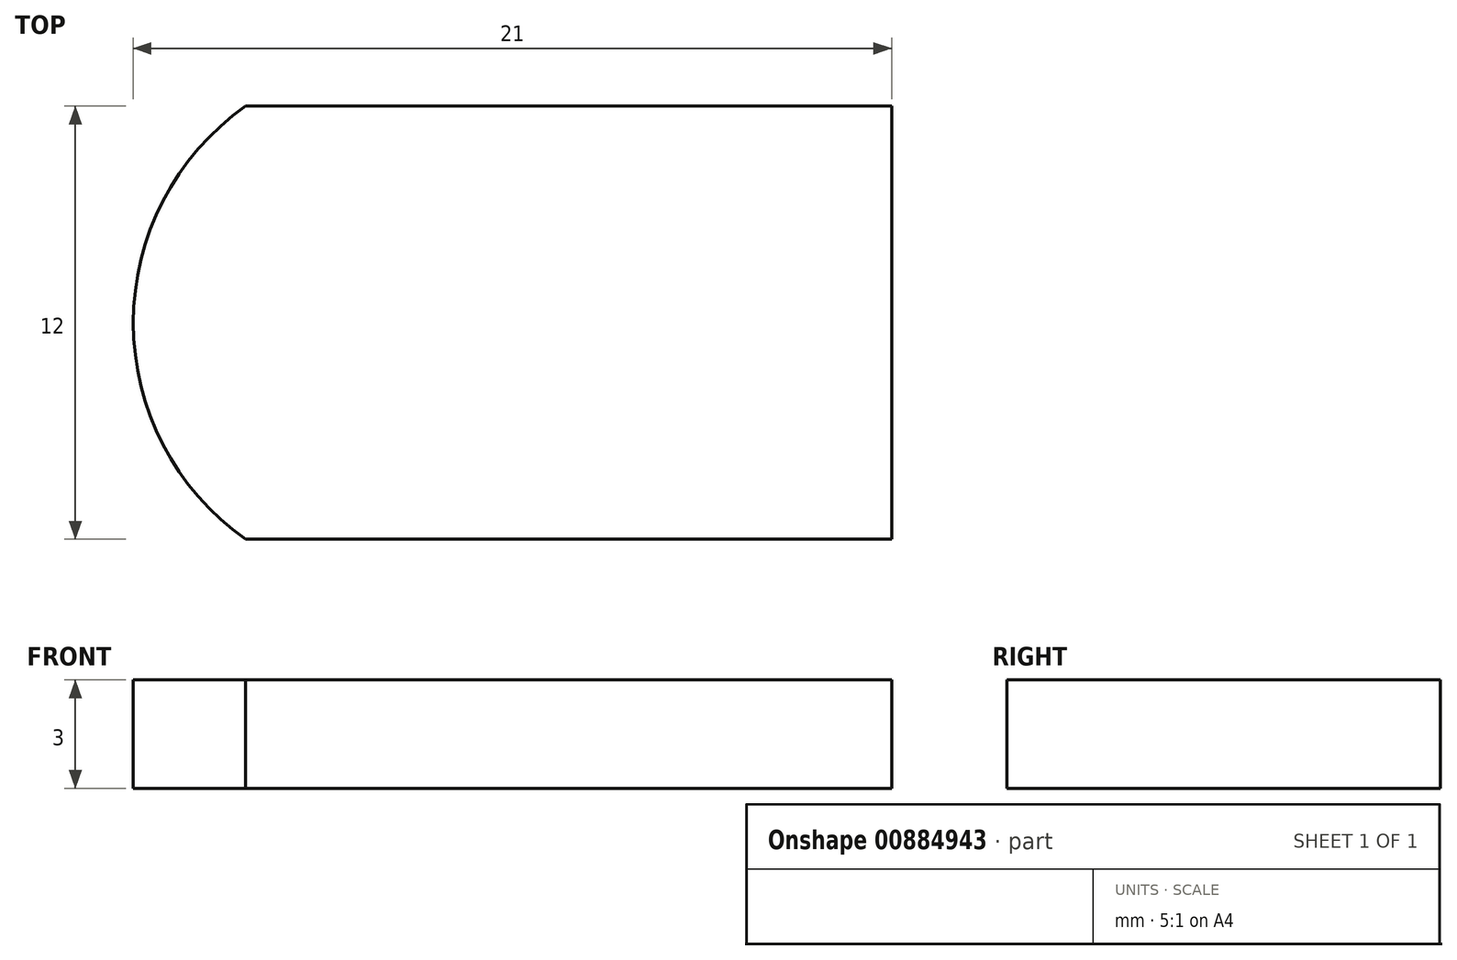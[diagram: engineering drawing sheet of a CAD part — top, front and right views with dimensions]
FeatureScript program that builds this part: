
annotation { "Feature Type Name" : "Feature", "Feature Type Description" : "" }
export const myFeature = defineFeature(function(context is Context, id is Id, definition is map)
    precondition{}
    {
        {
            var Q0;
            Q0=qCreatedBy(makeId("Top.planeOp"),FACE);
            var sketch = newSketch(context, id + "F0", { "sketchPlane" : qUnion([Q0])});
            skLineSegment(sketch, "E0.bottom", {"start": v(8.94, -6) * mm, "end": v(-8.94, -6) * mm});
            skLineSegment(sketch, "E0.top", {"start": v(8.94, 6) * mm, "end": v(-8.94, 6) * mm});
            skLineSegment(sketch, "E0.left", {"start": v(8.94, -6) * mm, "end": v(8.94, 6) * mm});
            skPoint(sketch, "E0.middle", {"position": v(0, 0) * mm});
            skArc(sketch, "E1", {"start": v(-8.94, 6) * mm, "mid": v(-12.06, 0) * mm, "end": v(-8.94, -6) * mm});
            skSolve(sketch);
        }
        {
            var Q0;
            Q0=makeQuery(id+"F0.imprint","IMPRINT",FACE,{"disambiguationData":[TD([[makeQuery(id+"F0.imprint","IMPRINT",EDGE,{"derivedFrom":sQuery(id+"F0.wireOp",EDGE,"E0.bottom")}),-1.0]])]});
            extrude(context, id + "F1", {"entities" : qUnion([Q0]), "depth" : 3 * mm, "offsetDistance" : 25 * mm});
        }
    });
